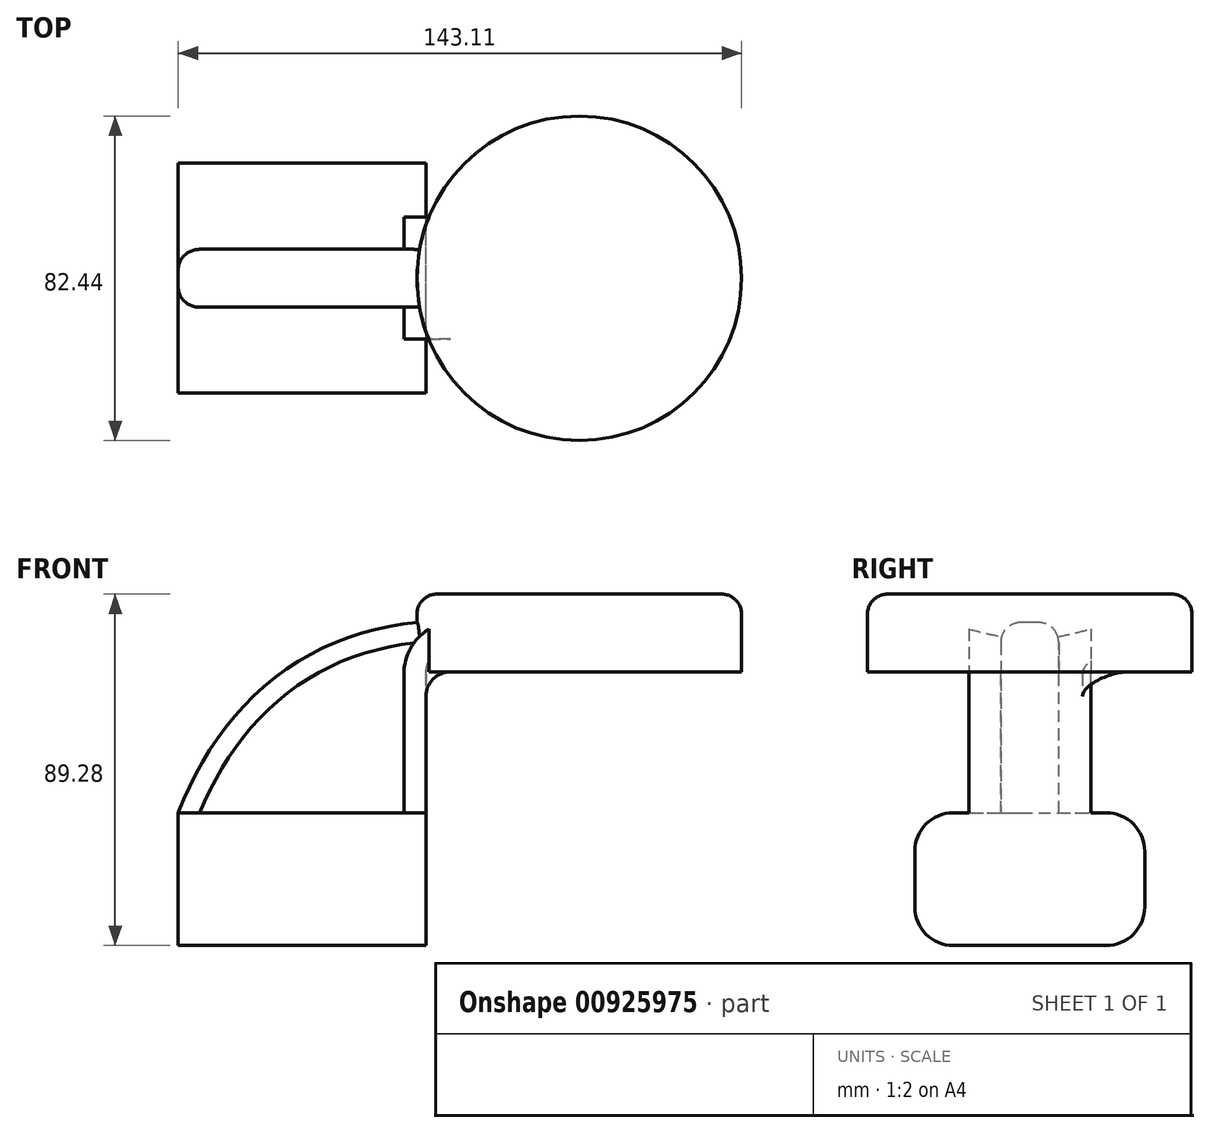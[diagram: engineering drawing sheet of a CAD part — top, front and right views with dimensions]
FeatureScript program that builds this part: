
annotation { "Feature Type Name" : "Feature", "Feature Type Description" : "" }
export const myFeature = defineFeature(function(context is Context, id is Id, definition is map)
    precondition{}
    {
        {
            var Q0;
            Q0=qCreatedBy(makeId("Front.planeOp"),FACE);
            var sketch = newSketch(context, id + "F0", { "sketchPlane" : qUnion([Q0])});
            skLineSegment(sketch, "E0.bottom", {"start": v(-31.45, -16.86) * mm, "end": v(31.45, -16.86) * mm});
            skLineSegment(sketch, "E0.top", {"start": v(-31.45, 16.86) * mm, "end": v(31.45, 16.86) * mm});
            skLineSegment(sketch, "E0.left", {"start": v(-31.45, -16.86) * mm, "end": v(-31.45, 16.86) * mm});
            skLineSegment(sketch, "E0.right", {"start": v(31.45, -16.86) * mm, "end": v(31.45, 16.86) * mm});
            skPoint(sketch, "E0.middle", {"position": v(0, 0) * mm});
            skLineSegment(sketch, "E1.bottom", {"start": v(55.76, 52.65) * mm, "end": v(111.66, 52.65) * mm});
            skLineSegment(sketch, "E1.top", {"start": v(55.76, 72.42) * mm, "end": v(111.66, 72.42) * mm});
            skLineSegment(sketch, "E1.left", {"start": v(55.76, 52.65) * mm, "end": v(55.76, 72.42) * mm});
            skLineSegment(sketch, "E1.right", {"start": v(111.66, 52.65) * mm, "end": v(111.66, 72.42) * mm});
            skPoint(sketch, "E1.middle", {"position": v(83.7, 62.53) * mm});
            skLineSegment(sketch, "E2", {"start": v(31.45, 16.86) * mm, "end": v(31.45, 52.07) * mm});
            skArc(sketch, "E3", {"start": v(39.35, 59.96) * mm, "mid": v(33.77, 57.65) * mm, "end": v(31.45, 52.07) * mm});
            skLineSegment(sketch, "E4", {"start": v(39.35, 59.96) * mm, "end": v(70.43, 59.96) * mm});
            skLineSegment(sketch, "E5.0", {"start": v(39.35, 65.55) * mm, "end": v(70.43, 65.55) * mm});
            skArc(sketch, "E5.1", {"start": v(39.35, 65.55) * mm, "mid": v(29.81, 61.6) * mm, "end": v(25.87, 52.07) * mm});
            skLineSegment(sketch, "E5.2", {"start": v(25.87, 12.85) * mm, "end": v(25.87, 52.07) * mm});
            skLineSegment(sketch, "E6", {"start": v(70.43, 52.65) * mm, "end": v(70.43, 72.42) * mm});
            skFitSpline(sketch, "E7", {"points": [v(-31.45, 16.86) * mm, v(39.35, 65.55) * mm], "startDerivative": vector(38.04, 97.2) * mm, "endDerivative": vector(98.19, -2.09) * mm});
            skSolve(sketch);
        }
        {
            var Q0;
            Q0=makeQuery(id+"F0.imprint","IMPRINT",FACE,{"disambiguationData":[TD([[makeQuery(id+"F0.imprint","IMPRINT",EDGE,{"derivedFrom":sQuery(id+"F0.wireOp",EDGE,"E0.bottom")}),1.0]])]});
            extrude(context, id + "F1", {"entities" : qUnion([Q0]), "endBound" : BoundingType.SYMMETRIC, "depth" : 58.42 * mm, "offsetDistance" : 25.4 * mm});
        }
        {
            var Q0;
            {var subQ1=sQuery(id+"F0.wireOp",EDGE,"E2");Q0=makeQuery(id+"F0.imprint","IMPRINT",FACE,{"disambiguationData":[TD([[makeQuery(id+"F0.imprint","IMPRINT",EDGE,{"derivedFrom":subQ1}),1.0]])]});}
            var Q1;
            {var subQ0=sQuery(id+"F0.wireOp",EDGE,"E4");var subQ1=sQuery(id+"F0.wireOp",EDGE,"E1.left");var subQ2=makeQuery(id+"F0.imprint","INTERSECT",VERTEX,{"derivedFrom":[subQ1,subQ0]});Q1=makeQuery(id+"F0.imprint","IMPRINT",FACE,{"disambiguationData":[TD([[makeQuery(id+"F0.imprint","IMPRINT",EDGE,{"disambiguationData":[TD([[subQ2,-1.0]])],"derivedFrom":subQ1}),-1.0]])]});}
            extrude(context, id + "F2", {"entities" : qUnion([Q0, Q1]), "operationType" : NewBodyOperationType.ADD, "endBound" : BoundingType.SYMMETRIC, "depth" : 30.99 * mm, "offsetDistance" : 25.4 * mm});
        }
        {
            var Q0;
            {var subQ4=sQuery(id+"F0.wireOp",EDGE,"E5.1");Q0=makeQuery(id+"F0.imprint","IMPRINT",FACE,{"disambiguationData":[TD([[makeQuery(id+"F0.imprint","IMPRINT",EDGE,{"derivedFrom":subQ4}),-1.0]])]});}
            extrude(context, id + "F3", {"entities" : qUnion([Q0]), "operationType" : NewBodyOperationType.ADD, "endBound" : BoundingType.SYMMETRIC, "depth" : 14.73 * mm, "offsetDistance" : 25.4 * mm});
        }
        {
            var Q0;
            {var subQ0=sQuery(id+"F0.wireOp",EDGE,"E1.right");Q0=makeQuery(id+"F0.imprint","IMPRINT",FACE,{"disambiguationData":[TD([[makeQuery(id+"F0.imprint","IMPRINT",EDGE,{"derivedFrom":subQ0}),1.0]])]});}
            var Q1;
            Q1=sQuery(id+"F0.wireOp",EDGE,"E6");
            revolve(context, id + "F4", {"operationType" : NewBodyOperationType.ADD, "surfaceOperationType" : NewSurfaceOperationType.NEW, "entities" : qUnion([Q0]), "axis" : qUnion([Q1]), "revolveType" : RevolveType.FULL});
        }
        {
            var Q0;
            Q0=makeQuery(id+"F1.opExtrude","CAP_EDGE",EDGE,{"disambiguationData":[OSD([sQuery(id+"F0.wireOp",EDGE,"E0.top")])],"isStart":false});
            var Q1;
            Q1=makeQuery(id+"F1.opExtrude","CAP_EDGE",EDGE,{"disambiguationData":[OSD([sQuery(id+"F0.wireOp",EDGE,"E0.top")])],"isStart":true});
            var Q2;
            Q2=makeQuery(id+"F1.opExtrude","CAP_EDGE",EDGE,{"disambiguationData":[OSD([sQuery(id+"F0.wireOp",EDGE,"E0.bottom")])],"isStart":true});
            var Q3;
            Q3=makeQuery(id+"F1.opExtrude","CAP_EDGE",EDGE,{"disambiguationData":[OSD([sQuery(id+"F0.wireOp",EDGE,"E0.bottom")])],"isStart":false});
            fillet(context, id + "F5", {"entities" : qUnion([Q0, Q1, Q2, Q3]), "radius" : 9.8 * mm, "tangentPropagation" : true, "allowEdgeOverflow" : false});
        }
        {
            var Q0;
            Q0=makeQuery(id+"F3.opExtrude","CAP_EDGE",EDGE,{"disambiguationData":[OSD([sQuery(id+"F0.wireOp",EDGE,"E7")])],"isStart":false});
            var Q1;
            Q1=makeQuery(id+"F3.opExtrude","CAP_EDGE",EDGE,{"disambiguationData":[OSD([sQuery(id+"F0.wireOp",EDGE,"E7")])],"isStart":true});
            fillet(context, id + "F6", {"entities" : qUnion([Q0, Q1]), "radius" : 5.08 * mm, "tangentPropagation" : true, "allowEdgeOverflow" : false});
        }
        {
            var Q0;
            Q0=makeQuery(id+"F4.opRevolve","SWEPT_EDGE",EDGE,{"disambiguationData":[OSD([sQuery(id+"F0.wireOp",EDGE,"E1.top"),sQuery(id+"F0.wireOp",EDGE,"E1.right")])]});
            fillet(context, id + "F7", {"entities" : qUnion([Q0]), "radius" : 5.08 * mm, "tangentPropagation" : true, "allowEdgeOverflow" : false});
        }
        {
            var Q0;
            Q0=makeQuery(id+"F4.boolean.opBoolean","INTERSECT",EDGE,{"derivedFrom":[makeQuery(id+"F2.opExtrude","SWEPT_FACE",FACE,{"disambiguationData":[OSD([sQuery(id+"F0.wireOp",EDGE,"E3")])]}),makeQuery(id+"F4.opRevolve","SWEPT_FACE",FACE,{"disambiguationData":[OSD([sQuery(id+"F0.wireOp",EDGE,"E1.bottom")])]})]});
            fillet(context, id + "F8", {"entities" : qUnion([Q0]), "radius" : 6.27 * mm, "tangentPropagation" : true, "allowEdgeOverflow" : false});
        }
    });
